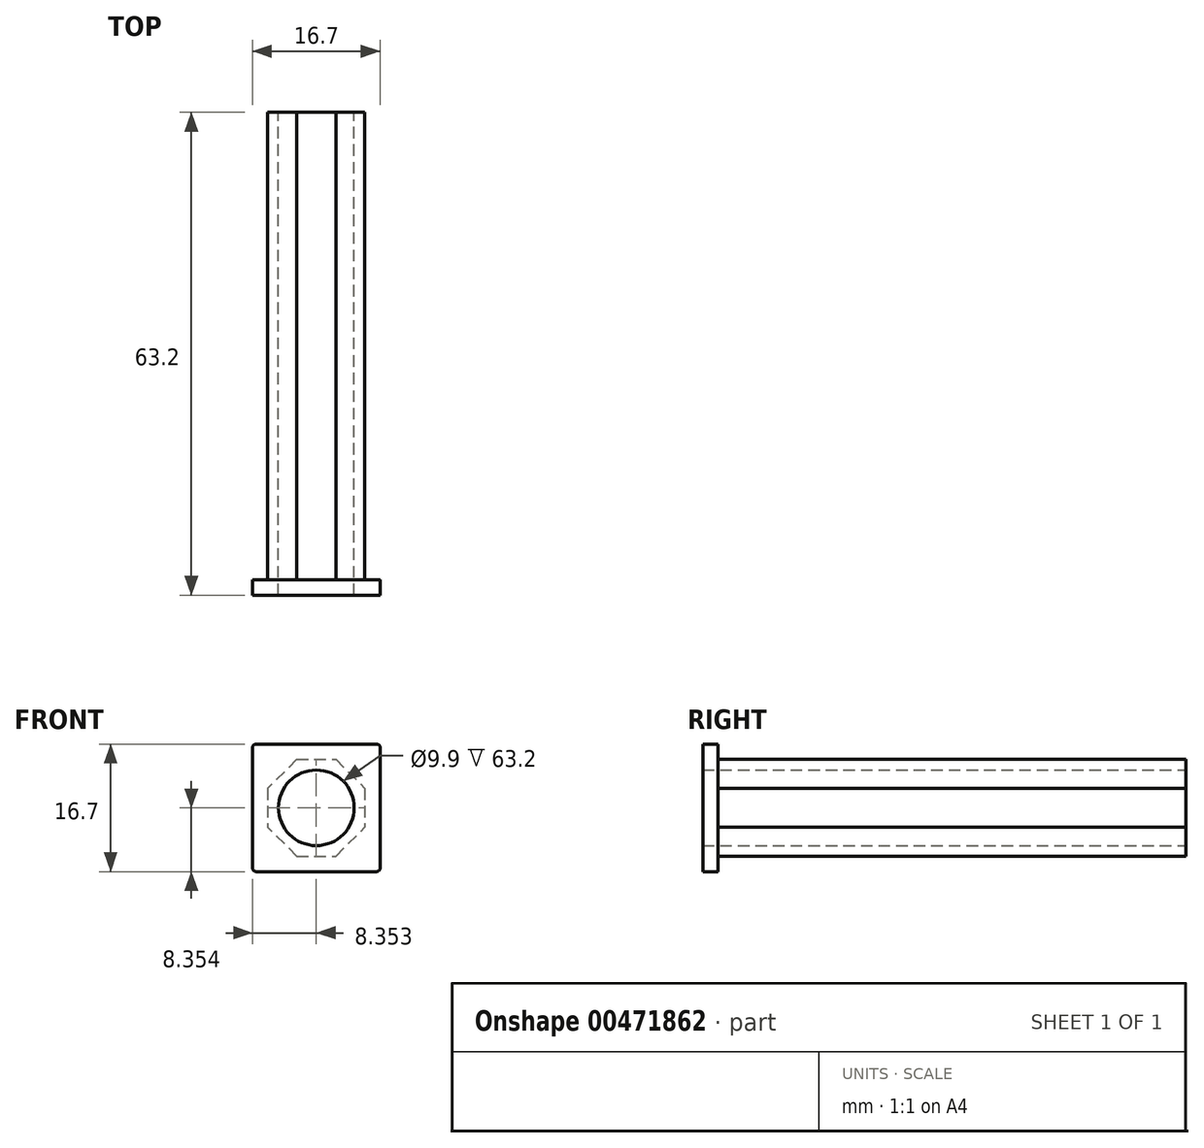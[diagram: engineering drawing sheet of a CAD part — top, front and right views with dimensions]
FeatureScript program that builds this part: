
annotation { "Feature Type Name" : "Feature", "Feature Type Description" : "" }
export const myFeature = defineFeature(function(context is Context, id is Id, definition is map)
    precondition{}
    {
        {
            var Q0;
            Q0=qCreatedBy(makeId("Front.planeOp"),FACE);
            var sketch = newSketch(context, id + "F0", { "sketchPlane" : qUnion([Q0])});
            skLineSegment(sketch, "E0.bottom", {"start": v(-8.6, 2.16) * mm, "end": v(4.1, 2.16) * mm});
            skLineSegment(sketch, "E0.top", {"start": v(-8.6, -10.54) * mm, "end": v(4.1, -10.54) * mm});
            skLineSegment(sketch, "E0.left", {"start": v(-8.6, 2.16) * mm, "end": v(-8.6, -10.54) * mm});
            skLineSegment(sketch, "E0.right", {"start": v(4.1, 2.16) * mm, "end": v(4.1, -10.54) * mm});
            skLineSegment(sketch, "E1.0", {"start": v(-10.6, 4.16) * mm, "end": v(-10.6, -12.54) * mm});
            skLineSegment(sketch, "E1.1", {"start": v(-10.6, 4.16) * mm, "end": v(6.1, 4.16) * mm});
            skLineSegment(sketch, "E1.2", {"start": v(6.1, 4.16) * mm, "end": v(6.1, -12.54) * mm});
            skLineSegment(sketch, "E1.3", {"start": v(-10.6, -12.54) * mm, "end": v(6.1, -12.54) * mm});
            skCircle(sketch, "E2", {"center": v(-2.26, -4.19) * mm, "radius": 4.95 * mm});
            skSolve(sketch);
        }
        {
            var Q0;
            Q0=makeQuery(id+"F0.imprint","IMPRINT",FACE,{"disambiguationData":[TD([[makeQuery(id+"F0.imprint","IMPRINT",EDGE,{"derivedFrom":sQuery(id+"F0.wireOp",EDGE,"E0.bottom")}),1.0]])]});
            var Q1;
            Q1=makeQuery(id+"F0.imprint","IMPRINT",FACE,{"disambiguationData":[TD([[makeQuery(id+"F0.imprint","IMPRINT",EDGE,{"derivedFrom":sQuery(id+"F0.wireOp",EDGE,"E0.bottom")}),-1.0]])]});
            extrude(context, id + "F1", {"entities" : qUnion([Q0, Q1]), "depth" : 2 * mm});
        }
        {
            var Q0;
            Q0=makeQuery(id+"F0.imprint","IMPRINT",FACE,{"disambiguationData":[TD([[makeQuery(id+"F0.imprint","IMPRINT",EDGE,{"derivedFrom":sQuery(id+"F0.wireOp",EDGE,"E0.bottom")}),-1.0]])]});
            extrude(context, id + "F2", {"entities" : qUnion([Q0]), "operationType" : NewBodyOperationType.ADD, "depth" : -61.2 * mm});
        }
        {
            var Q0;
            Q0=makeQuery(id+"F1.opExtrude","SWEPT_EDGE",EDGE,{"disambiguationData":[OSD([sQuery(id+"F0.wireOp",EDGE,"E1.0"),sQuery(id+"F0.wireOp",EDGE,"E1.1")])]});
            var Q1;
            Q1=makeQuery(id+"F1.opExtrude","SWEPT_EDGE",EDGE,{"disambiguationData":[OSD([sQuery(id+"F0.wireOp",EDGE,"E1.1"),sQuery(id+"F0.wireOp",EDGE,"E1.2")])]});
            var Q2;
            Q2=makeQuery(id+"F1.opExtrude","SWEPT_EDGE",EDGE,{"disambiguationData":[OSD([sQuery(id+"F0.wireOp",EDGE,"E1.2"),sQuery(id+"F0.wireOp",EDGE,"E1.3")])]});
            var Q3;
            Q3=makeQuery(id+"F1.opExtrude","SWEPT_EDGE",EDGE,{"disambiguationData":[OSD([sQuery(id+"F0.wireOp",EDGE,"E1.0"),sQuery(id+"F0.wireOp",EDGE,"E1.3")])]});
            fillet(context, id + "F3", {"entities" : qUnion([Q0, Q1, Q2, Q3]), "radius" : 0.5 * mm, "tangentPropagation" : true, "allowEdgeOverflow" : false});
        }
        {
            var Q0;
            Q0=makeQuery(id+"F2.opExtrude","SWEPT_EDGE",EDGE,{"disambiguationData":[OSD([sQuery(id+"F0.wireOp",EDGE,"E0.top"),sQuery(id+"F0.wireOp",EDGE,"E0.left")])]});
            var Q1;
            Q1=makeQuery(id+"F2.opExtrude","SWEPT_EDGE",EDGE,{"disambiguationData":[OSD([sQuery(id+"F0.wireOp",EDGE,"E0.bottom"),sQuery(id+"F0.wireOp",EDGE,"E0.left")])]});
            var Q2;
            Q2=makeQuery(id+"F2.opExtrude","SWEPT_EDGE",EDGE,{"disambiguationData":[OSD([sQuery(id+"F0.wireOp",EDGE,"E0.top"),sQuery(id+"F0.wireOp",EDGE,"E0.right")])]});
            var Q3;
            Q3=makeQuery(id+"F2.opExtrude","SWEPT_EDGE",EDGE,{"disambiguationData":[OSD([sQuery(id+"F0.wireOp",EDGE,"E0.bottom"),sQuery(id+"F0.wireOp",EDGE,"E0.right")])]});
            chamfer(context, id + "F4", {"entities" : qUnion([Q0, Q1, Q2, Q3]), "width" : 3.8 * mm, "tangentPropagation" : true});
        }
    });
